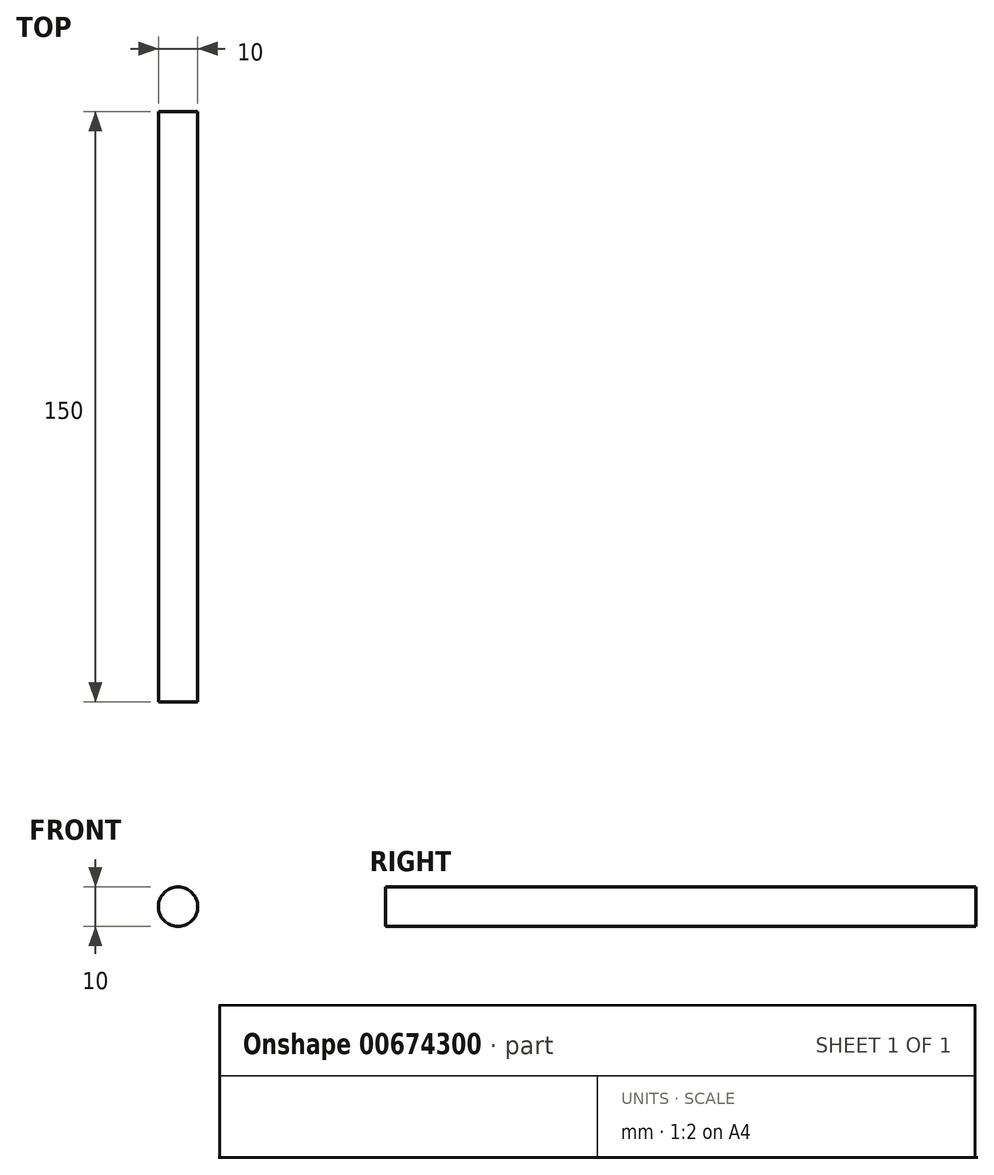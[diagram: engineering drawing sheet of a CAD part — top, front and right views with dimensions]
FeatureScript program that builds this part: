
annotation { "Feature Type Name" : "Feature", "Feature Type Description" : "" }
export const myFeature = defineFeature(function(context is Context, id is Id, definition is map)
    precondition{}
    {
        {
            var Q0;
            Q0=qCreatedBy(makeId("Front.planeOp"),FACE);
            var sketch = newSketch(context, id + "F0", { "sketchPlane" : qUnion([Q0])});
            skCircle(sketch, "E0", {"center": v(-77.05, 7.15) * mm, "radius": 5 * mm});
            skSolve(sketch);
        }
        {
            var Q0;
            Q0 = qSketchRegion(id + "F0", true);
            extrude(context, id + "F1", {"entities" : qUnion([Q0]), "depth" : 150 * mm, "offsetDistance" : 25 * mm});
        }
    });
